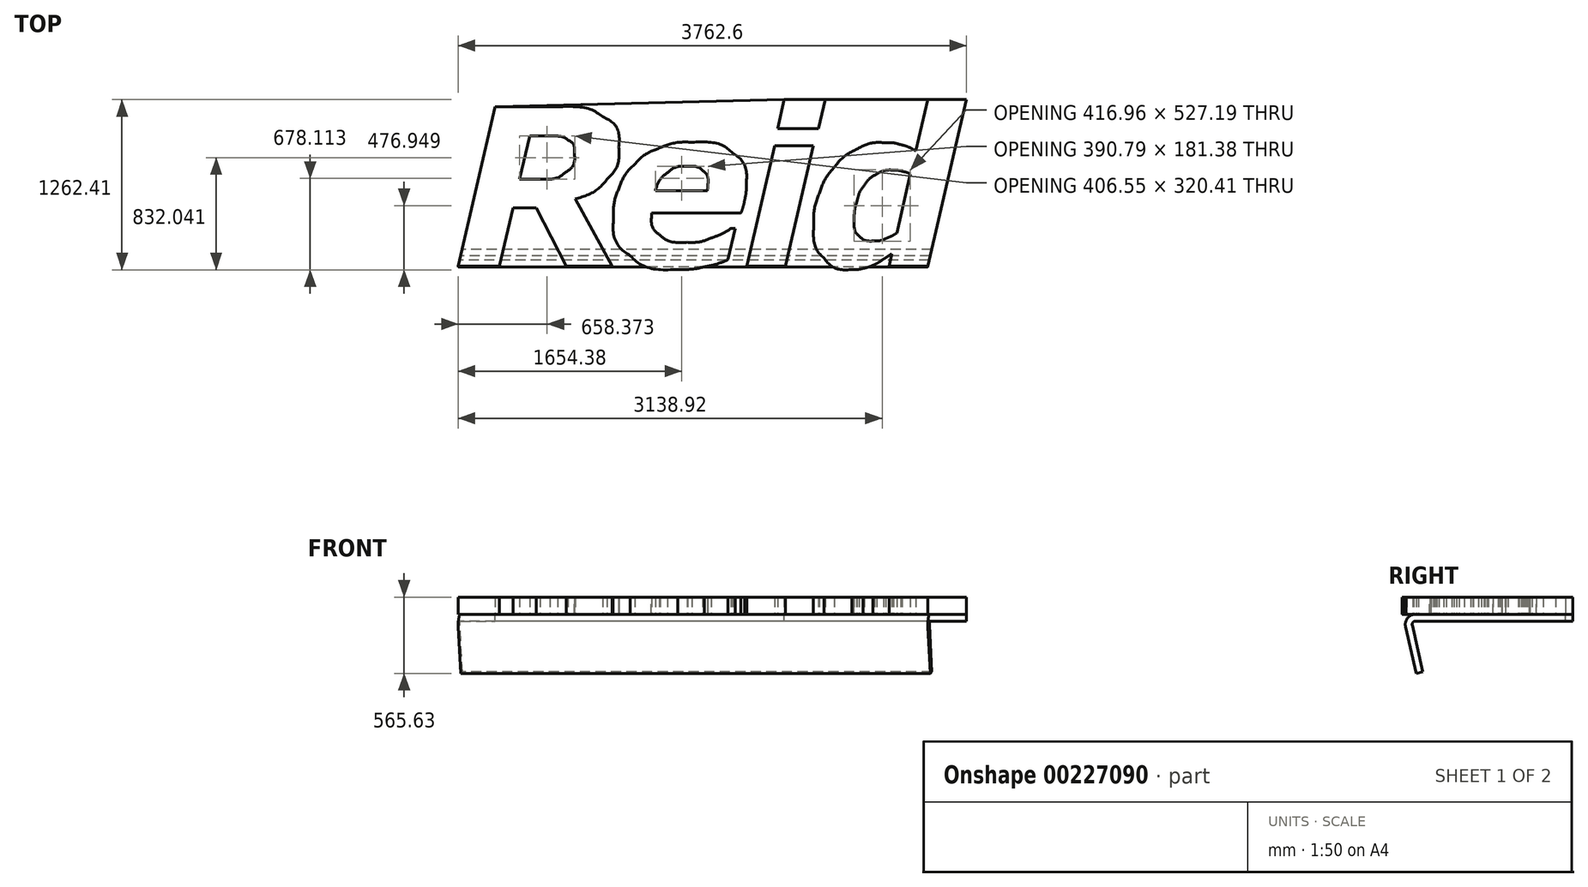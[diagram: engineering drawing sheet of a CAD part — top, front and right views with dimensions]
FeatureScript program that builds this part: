
annotation { "Feature Type Name" : "Feature", "Feature Type Description" : "" }
export const myFeature = defineFeature(function(context is Context, id is Id, definition is map)
    precondition{}
    {
        {
            var Q0;
            Q0=qCreatedBy(makeId("Top.planeOp"),FACE);
            var sketch = newSketch(context, id + "F0", { "sketchPlane" : qUnion([Q0])});
            skFitSpline(sketch, "E0", {"points": [v(-1021.9, 228.2) * mm, v(-1021.9, 275.83) * mm, v(-1037.24, 309.43) * mm, v(-1067.93, 329) * mm]});
            skFitSpline(sketch, "E1", {"points": [v(-1067.93, 329) * mm, v(-1098.1, 349.12) * mm, v(-1142.8, 359.17) * mm, v(-1202.07, 359.17) * mm]});
            skFitSpline(sketch, "E2", {"points": [v(-1276.69, 40.88) * mm, v(-1195.72, 40.88) * mm, v(-1133.02, 57.28) * mm, v(-1088.57, 90.1) * mm]});
            skFitSpline(sketch, "E3", {"points": [v(-1088.57, 90.1) * mm, v(-1044.12, 123.43) * mm, v(-1021.9, 169.47) * mm, v(-1021.9, 228.2) * mm]});
            skLineSegment(sketch, "E4", {"start": v(-1202.07, 359.17) * mm, "end": v(-1352.89, 359.17) * mm});
            skLineSegment(sketch, "E5", {"start": v(-1352.89, 359.17) * mm, "end": v(-1426.7, 40.88) * mm});
            skLineSegment(sketch, "E6", {"start": v(-1426.7, 40.88) * mm, "end": v(-1276.69, 40.88) * mm});
            skFitSpline(sketch, "E7", {"points": [v(-693.28, 279) * mm, v(-693.28, 184.28) * mm, v(-722.12, 104.64) * mm, v(-779.8, 40.08) * mm]});
            skFitSpline(sketch, "E8", {"points": [v(-779.8, 40.08) * mm, v(-837.48, -24.47) * mm, v(-915.8, -73.16) * mm, v(-1014.75, -105.97) * mm]});
            skFitSpline(sketch, "E9", {"points": [v(-1146.51, 576.66) * mm, v(-1002.05, 576.66) * mm, v(-890.4, 552.05) * mm, v(-811.55, 502.84) * mm]});
            skFitSpline(sketch, "E10", {"points": [v(-811.55, 502.84) * mm, v(-732.7, 454.16) * mm, v(-693.28, 379.54) * mm, v(-693.28, 279) * mm]});
            skLineSegment(sketch, "E11", {"start": v(-1014.75, -105.97) * mm, "end": v(-741.7, -605.23) * mm});
            skLineSegment(sketch, "E12", {"start": v(-741.7, -605.23) * mm, "end": v(-1082.22, -605.23) * mm});
            skLineSegment(sketch, "E13", {"start": v(-1082.22, -605.23) * mm, "end": v(-1304.47, -171.85) * mm});
            skLineSegment(sketch, "E14", {"start": v(-1304.47, -171.85) * mm, "end": v(-1475.92, -171.85) * mm});
            skLineSegment(sketch, "E15", {"start": v(-1475.92, -171.85) * mm, "end": v(-1575.93, -605.23) * mm});
            skLineSegment(sketch, "E16", {"start": v(-1575.93, -605.23) * mm, "end": v(-1880.73, -605.23) * mm});
            skLineSegment(sketch, "E17", {"start": v(-1880.73, -605.23) * mm, "end": v(-1607.68, 576.66) * mm});
            skLineSegment(sketch, "E18", {"start": v(-1607.68, 576.66) * mm, "end": v(-1146.51, 576.66) * mm});
            skFitSpline(sketch, "E19", {"points": [v(-256.12, -629.05) * mm, v(-408, -629.05) * mm, v(-525.2, -595.44) * mm, v(-607.75, -528.24) * mm]});
            skFitSpline(sketch, "E20", {"points": [v(-607.75, -528.24) * mm, v(-690.3, -461.04) * mm, v(-731.58, -368.17) * mm, v(-731.58, -249.63) * mm]});
            skFitSpline(sketch, "E21", {"points": [v(-731.58, -249.63) * mm, v(-731.58, -168.67) * mm, v(-718.08, -94.32) * mm, v(-691.1, -26.6) * mm]});
            skFitSpline(sketch, "E22", {"points": [v(-691.1, -26.6) * mm, v(-664.1, 41.14) * mm, v(-625.21, 100.67) * mm, v(-574.41, 152) * mm]});
            skFitSpline(sketch, "E23", {"points": [v(-574.41, 152) * mm, v(-525.73, 201.74) * mm, v(-464.88, 241.17) * mm, v(-391.85, 270.27) * mm]});
            skFitSpline(sketch, "E24", {"points": [v(-391.85, 270.27) * mm, v(-318.83, 299.38) * mm, v(-238.66, 313.93) * mm, v(-151.34, 313.93) * mm]});
            skFitSpline(sketch, "E25", {"points": [v(-151.34, 313.93) * mm, v(-18.52, 313.93) * mm, v(81.49, 286.94) * mm, v(148.7, 232.97) * mm]});
            skFitSpline(sketch, "E26", {"points": [v(148.7, 232.97) * mm, v(216.43, 179.52) * mm, v(250.3, 100.4) * mm, v(250.3, -4.37) * mm]});
            skFitSpline(sketch, "E27", {"points": [v(250.3, -4.37) * mm, v(250.3, -40.35) * mm, v(246.59, -75.54) * mm, v(239.18, -109.93) * mm]});
            skFitSpline(sketch, "E28", {"points": [v(239.18, -109.93) * mm, v(232.3, -144.33) * mm, v(223.04, -178.46) * mm, v(211.4, -212.33) * mm]});
            skFitSpline(sketch, "E29", {"points": [v(-450.59, -212.33) * mm, v(-450.59, -215.5) * mm, v(-450.59, -218.68) * mm, v(-450.59, -221.85) * mm]});
            skFitSpline(sketch, "E30", {"points": [v(-450.59, -221.85) * mm, v(-450.59, -224.5) * mm, v(-450.59, -227.4) * mm, v(-450.59, -230.58) * mm]});
            skFitSpline(sketch, "E31", {"points": [v(-450.59, -230.58) * mm, v(-450.59, -292.5) * mm, v(-428.9, -340.92) * mm, v(-385.5, -375.84) * mm]});
            skFitSpline(sketch, "E32", {"points": [v(-385.5, -375.84) * mm, v(-342.1, -410.77) * mm, v(-275.7, -428.23) * mm, v(-186.27, -428.23) * mm]});
            skFitSpline(sketch, "E33", {"points": [v(-186.27, -428.23) * mm, v(-123.83, -428.23) * mm, v(-64.83, -417.64) * mm, v(-9.26, -396.48) * mm]});
            skFitSpline(sketch, "E34", {"points": [v(-9.26, -396.48) * mm, v(46.83, -375.31) * mm, v(95.51, -351.76) * mm, v(136.79, -325.83) * mm]});
            skLineSegment(sketch, "E35", {"start": v(211.4, -212.33) * mm, "end": v(-450.59, -212.33) * mm});
            skLineSegment(sketch, "E36", {"start": v(-450.59, -212.33) * mm, "end": v(211.4, -212.33) * mm});
            skFitSpline(sketch, "E37", {"points": [v(115.36, -555.23) * mm, v(59.8, -579.57) * mm, v(1.32, -597.83) * mm, v(-60.06, -610) * mm]});
            skFitSpline(sketch, "E38", {"points": [v(-60.06, -610) * mm, v(-121.45, -622.7) * mm, v(-186.8, -629.05) * mm, v(-256.12, -629.05) * mm]});
            skLineSegment(sketch, "E39", {"start": v(136.79, -325.83) * mm, "end": v(168.54, -325.83) * mm});
            skLineSegment(sketch, "E40", {"start": v(168.54, -325.83) * mm, "end": v(115.36, -555.23) * mm});
            skFitSpline(sketch, "E41", {"points": [v(-37.84, -44.85) * mm, v(-36.25, -35.32) * mm, v(-35.2, -26.6) * mm, v(-34.66, -18.65) * mm]});
            skFitSpline(sketch, "E42", {"points": [v(-34.66, -18.65) * mm, v(-33.6, -10.72) * mm, v(-33.08, -2.51) * mm, v(-33.08, 5.95) * mm]});
            skFitSpline(sketch, "E43", {"points": [v(-33.08, 5.95) * mm, v(-33.08, 47.76) * mm, v(-46.04, 79.77) * mm, v(-71.97, 102) * mm]});
            skFitSpline(sketch, "E44", {"points": [v(-71.97, 102) * mm, v(-97.9, 124.22) * mm, v(-135.2, 135.33) * mm, v(-183.89, 135.33) * mm]});
            skFitSpline(sketch, "E45", {"points": [v(-183.89, 135.33) * mm, v(-242.63, 135.33) * mm, v(-292.1, 119.46) * mm, v(-332.32, 87.7) * mm]});
            skFitSpline(sketch, "E46", {"points": [v(-332.32, 87.7) * mm, v(-372, 55.96) * mm, v(-402.17, 11.77) * mm, v(-422.8, -44.85) * mm]});
            skLineSegment(sketch, "E47", {"start": v(-422.8, -44.85) * mm, "end": v(-37.84, -44.85) * mm});
            skLineSegment(sketch, "E48", {"start": v(-37.84, -44.85) * mm, "end": v(-37.84, -44.85) * mm});
            skLineSegment(sketch, "E49", {"start": v(-37.84, -44.85) * mm, "end": v(-422.8, -44.85) * mm});
            skLineSegment(sketch, "E50", {"start": v(834.88, 629.84) * mm, "end": v(784.87, 413.15) * mm});
            skLineSegment(sketch, "E51", {"start": v(784.87, 413.15) * mm, "end": v(481.66, 413.15) * mm});
            skLineSegment(sketch, "E52", {"start": v(481.66, 413.15) * mm, "end": v(531.67, 629.84) * mm});
            skLineSegment(sketch, "E53", {"start": v(531.67, 629.84) * mm, "end": v(834.88, 629.84) * mm});
            skFitSpline(sketch, "E54", {"points": [v(1465.6, 78.18) * mm, v(1450.25, 85.6) * mm, v(1430.14, 92.2) * mm, v(1405.27, 98.03) * mm]});
            skFitSpline(sketch, "E55", {"points": [v(1405.27, 98.03) * mm, v(1380.4, 104.38) * mm, v(1358.44, 107.55) * mm, v(1339.4, 107.55) * mm]});
            skFitSpline(sketch, "E56", {"points": [v(1339.4, 107.55) * mm, v(1293.88, 107.55) * mm, v(1252.87, 97.5) * mm, v(1216.36, 77.4) * mm]});
            skFitSpline(sketch, "E57", {"points": [v(1216.36, 77.4) * mm, v(1179.85, 57.28) * mm, v(1148.9, 29.77) * mm, v(1123.5, -5.16) * mm]});
            skFitSpline(sketch, "E58", {"points": [v(1123.5, -5.16) * mm, v(1100.74, -36.38) * mm, v(1082.75, -76.33) * mm, v(1069.52, -125.02) * mm]});
            skFitSpline(sketch, "E59", {"points": [v(1069.52, -125.02) * mm, v(1056.29, -173.17) * mm, v(1049.67, -219.74) * mm, v(1049.67, -264.72) * mm]});
            skFitSpline(sketch, "E60", {"points": [v(1049.67, -264.72) * mm, v(1049.67, -318.16) * mm, v(1062.1, -357.06) * mm, v(1086.98, -381.4) * mm]});
            skFitSpline(sketch, "E61", {"points": [v(1086.98, -381.4) * mm, v(1111.85, -405.74) * mm, v(1149.69, -417.9) * mm, v(1200.49, -417.9) * mm]});
            skFitSpline(sketch, "E62", {"points": [v(1200.49, -417.9) * mm, v(1226.42, -417.9) * mm, v(1253.67, -412.09) * mm, v(1282.24, -400.45) * mm]});
            skFitSpline(sketch, "E63", {"points": [v(1282.24, -400.45) * mm, v(1311.35, -388.8) * mm, v(1338.86, -375.05) * mm, v(1364.8, -359.17) * mm]});
            skLineSegment(sketch, "E64", {"start": v(747.57, 286.15) * mm, "end": v(541.2, -605.23) * mm});
            skLineSegment(sketch, "E65", {"start": v(541.2, -605.23) * mm, "end": v(253.85, -605.23) * mm});
            skLineSegment(sketch, "E66", {"start": v(253.85, -605.23) * mm, "end": v(460.23, 286.15) * mm});
            skLineSegment(sketch, "E67", {"start": v(460.23, 286.15) * mm, "end": v(747.57, 286.15) * mm});
            skLineSegment(sketch, "E68", {"start": v(1364.8, -359.17) * mm, "end": v(1465.6, 78.18) * mm});
            skLineSegment(sketch, "E69", {"start": v(1465.6, 78.18) * mm, "end": v(1364.8, -359.17) * mm});
            skFitSpline(sketch, "E70", {"points": [v(1329.07, -512.37) * mm, v(1301.56, -529.83) * mm, v(1277.22, -545.7) * mm, v(1256.05, -560) * mm]});
            skFitSpline(sketch, "E71", {"points": [v(1256.05, -560) * mm, v(1235.41, -573.75) * mm, v(1212.4, -586.45) * mm, v(1187, -598.1) * mm]});
            skFitSpline(sketch, "E72", {"points": [v(1187, -598.1) * mm, v(1163.18, -608.67) * mm, v(1139.63, -616.61) * mm, v(1116.35, -621.9) * mm]});
            skFitSpline(sketch, "E73", {"points": [v(1116.35, -621.9) * mm, v(1093.6, -627.2) * mm, v(1066.08, -629.84) * mm, v(1033.8, -629.84) * mm]});
            skFitSpline(sketch, "E74", {"points": [v(1033.8, -629.84) * mm, v(947.54, -629.84) * mm, v(878.49, -601.8) * mm, v(826.63, -545.7) * mm]});
            skFitSpline(sketch, "E75", {"points": [v(826.63, -545.7) * mm, v(775.3, -489.61) * mm, v(749.64, -409.97) * mm, v(749.64, -306.78) * mm]});
            skFitSpline(sketch, "E76", {"points": [v(749.64, -306.78) * mm, v(749.64, -222.12) * mm, v(763.13, -142.74) * mm, v(790.12, -68.66) * mm]});
            skFitSpline(sketch, "E77", {"points": [v(790.12, -68.66) * mm, v(817.63, 5.95) * mm, v(855.2, 71.83) * mm, v(902.83, 128.98) * mm]});
            skFitSpline(sketch, "E78", {"points": [v(902.83, 128.98) * mm, v(949.4, 184.55) * mm, v(1004.43, 228.73) * mm, v(1067.93, 261.54) * mm]});
            skFitSpline(sketch, "E79", {"points": [v(1067.93, 261.54) * mm, v(1131.43, 294.35) * mm, v(1197.84, 310.75) * mm, v(1267.16, 310.75) * mm]});
            skFitSpline(sketch, "E80", {"points": [v(1267.16, 310.75) * mm, v(1315.84, 310.75) * mm, v(1358.18, 305.73) * mm, v(1394.16, 295.67) * mm]});
            skFitSpline(sketch, "E81", {"points": [v(1394.16, 295.67) * mm, v(1430.14, 286.15) * mm, v(1467.19, 271.07) * mm, v(1505.29, 250.43) * mm]});
            skLineSegment(sketch, "E82", {"start": v(1880.73, 629.84) * mm, "end": v(1594.98, -605.23) * mm});
            skLineSegment(sketch, "E83", {"start": v(1594.98, -605.23) * mm, "end": v(1307.64, -605.23) * mm});
            skLineSegment(sketch, "E84", {"start": v(1307.64, -605.23) * mm, "end": v(1329.07, -512.37) * mm});
            skLineSegment(sketch, "E85", {"start": v(1505.29, 250.43) * mm, "end": v(1593.4, 629.84) * mm});
            skLineSegment(sketch, "E86", {"start": v(1593.4, 629.84) * mm, "end": v(1880.73, 629.84) * mm});
            skSolve(sketch);
        }
        {
            var Q0;
            Q0=makeQuery(id+"F0.imprint","IMPRINT",FACE,{"disambiguationData":[TD([[makeQuery(id+"F0.imprint","IMPRINT",EDGE,{"derivedFrom":sQuery(id+"F0.wireOp",EDGE,"E0")}),-1.0]])]});
            var Q1;
            Q1=makeQuery(id+"F0.imprint","IMPRINT",FACE,{"disambiguationData":[TD([[makeQuery(id+"F0.imprint","IMPRINT",EDGE,{"derivedFrom":sQuery(id+"F0.wireOp",EDGE,"E19")}),-1.0]])]});
            var Q2;
            Q2=makeQuery(id+"F0.imprint","IMPRINT",FACE,{"disambiguationData":[TD([[makeQuery(id+"F0.imprint","IMPRINT",EDGE,{"derivedFrom":sQuery(id+"F0.wireOp",EDGE,"E64")}),-1.0]])]});
            var Q3;
            Q3=makeQuery(id+"F0.imprint","IMPRINT",FACE,{"disambiguationData":[TD([[makeQuery(id+"F0.imprint","IMPRINT",EDGE,{"derivedFrom":sQuery(id+"F0.wireOp",EDGE,"E50")}),-1.0]])]});
            var Q4;
            Q4=makeQuery(id+"F0.imprint","IMPRINT",FACE,{"disambiguationData":[TD([[makeQuery(id+"F0.imprint","IMPRINT",EDGE,{"derivedFrom":sQuery(id+"F0.wireOp",EDGE,"E54")}),-1.0]])]});
            extrude(context, id + "F1", {"entities" : qUnion([Q0, Q1, Q2, Q3, Q4]), "depth" : 127 * mm});
        }
        {
            var Q0;
            Q0=qCreatedBy(makeId("Right.planeOp"),FACE);
            var sketch = newSketch(context, id + "F2", { "sketchPlane" : qUnion([Q0])});
            skLineSegment(sketch, "E87", {"start": v(630.14, 0) * mm, "end": v(-533.66, 0) * mm});
            skLineSegment(sketch, "E88", {"start": v(-607.97, -93.07) * mm, "end": v(-529.53, -438.63) * mm});
            skPoint(sketch, "E89.visualSharp", {"position": v(-629.1, 0) * mm});
            skArc(sketch, "E89.filletArc", {"start": v(-533.66, 0) * mm, "mid": v(-593.2, -28.65) * mm, "end": v(-607.97, -93.07) * mm});
            skLineSegment(sketch, "E90.0", {"start": v(-558.43, -81.82) * mm, "end": v(-479.99, -427.39) * mm});
            skArc(sketch, "E90.1", {"start": v(-533.66, -50.8) * mm, "mid": v(-553.51, -60.35) * mm, "end": v(-558.43, -81.82) * mm});
            skLineSegment(sketch, "E90.2", {"start": v(630.14, -50.8) * mm, "end": v(-533.66, -50.8) * mm});
            skLineSegment(sketch, "E91", {"start": v(-529.53, -438.63) * mm, "end": v(-479.99, -427.39) * mm});
            skLineSegment(sketch, "E92", {"start": v(630.14, 0) * mm, "end": v(630.14, -50.8) * mm});
            skSolve(sketch);
        }
        {
            var Q0;
            Q0=makeQuery(id+"F2.imprint","IMPRINT",FACE,{"disambiguationData":[TD([[makeQuery(id+"F2.imprint","IMPRINT",EDGE,{"derivedFrom":sQuery(id+"F2.wireOp",EDGE,"E87")}),1.0]])]});
            var Q1;
            Q1=makeQuery(id+"F1.opExtrude","SWEPT_FACE",FACE,{"disambiguationData":[OSD([sQuery(id+"F0.wireOp",EDGE,"E82")])]});
            var Q2;
            Q2=makeQuery(id+"F1.opExtrude","SWEPT_FACE",FACE,{"disambiguationData":[OSD([sQuery(id+"F0.wireOp",EDGE,"E17")])]});
            extrude(context, id + "F3", {"entities" : qUnion([Q0]), "endBound" : BoundingType.UP_TO_SURFACE, "endBoundEntityFace" : qUnion([Q1]), "depth" : 25.4 * mm, "hasSecondDirection" : true, "secondDirectionBound" : SecondDirectionBoundingType.UP_TO_SURFACE, "secondDirectionOppositeDirection" : true, "secondDirectionBoundEntityFace" : qUnion([Q2]), "secondDirectionDepth" : 25.4 * mm});
        }
        {
            var Q0;
            Q0=makeQuery(id+"F3.opExtrude","SWEPT_FACE",FACE,{"disambiguationData":[OSD([sQuery(id+"F2.wireOp",EDGE,"E87")])]});
            var sketch = newSketch(context, id + "F4", { "sketchPlane" : qUnion([Q0])});
            skLineSegment(sketch, "E93", {"start": v(531.77, 630.14) * mm, "end": v(-1607.71, 576.5) * mm});
            skLineSegment(sketch, "E94", {"start": v(-1607.71, 576.5) * mm, "end": v(-1595.32, 630.14) * mm});
            skLineSegment(sketch, "E95", {"start": v(-1595.32, 630.14) * mm, "end": v(531.77, 630.14) * mm});
            skSolve(sketch);
        }
        {
            var Q0;
            Q0=makeQuery(id+"F4.imprint","IMPRINT",FACE,{"disambiguationData":[TD([[makeQuery(id+"F4.imprint","IMPRINT",EDGE,{"derivedFrom":sQuery(id+"F4.wireOp",EDGE,"E93")}),-1.0]])]});
            var Q1;
            Q1=makeQuery(id+"F3.opExtrude","SWEPT_FACE",FACE,{"disambiguationData":[OSD([sQuery(id+"F2.wireOp",EDGE,"E90.2")])]});
            extrude(context, id + "F5", {"entities" : qUnion([Q0]), "endBound" : BoundingType.UP_TO_SURFACE, "oppositeDirection" : true, "endBoundEntityFace" : qUnion([Q1]), "depth" : 25.4 * mm});
        }
        {
            var Q0;
            Q0=makeQuery(id+"F5.opExtrude","SWEPT_BODY",BODY,{"disambiguationData":[OSD([sQuery(id+"F4.wireOp",EDGE,"E93"),sQuery(id+"F4.wireOp",EDGE,"E94"),sQuery(id+"F4.wireOp",EDGE,"E95")])]});
            var Q1;
            Q1=makeQuery(id+"F3.opExtrude","SWEPT_BODY",BODY,{"disambiguationData":[OSD([sQuery(id+"F2.wireOp",EDGE,"E87"),sQuery(id+"F2.wireOp",EDGE,"E88"),sQuery(id+"F2.wireOp",EDGE,"E89.filletArc"),sQuery(id+"F2.wireOp",EDGE,"E90.0"),sQuery(id+"F2.wireOp",EDGE,"E90.1"),sQuery(id+"F2.wireOp",EDGE,"E90.2"),sQuery(id+"F2.wireOp",EDGE,"E91"),sQuery(id+"F2.wireOp",EDGE,"E92")])]});
            booleanBodies(context, id + "F6", {"operationType" : BooleanOperationType.SUBTRACTION, "tools" : qUnion([Q0]), "targets" : qUnion([Q1])});
        }
    });
